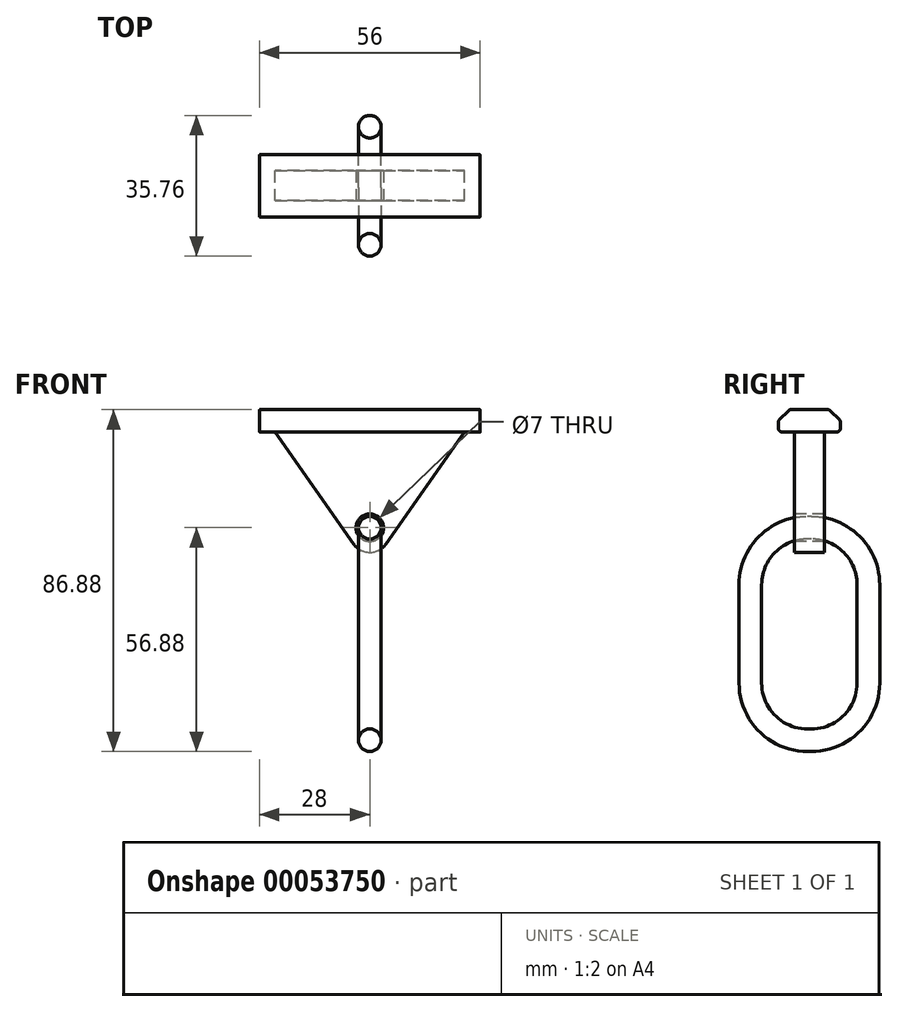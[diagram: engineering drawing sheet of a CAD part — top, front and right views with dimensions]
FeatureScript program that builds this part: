
annotation { "Feature Type Name" : "Feature", "Feature Type Description" : "" }
export const myFeature = defineFeature(function(context is Context, id is Id, definition is map)
    precondition{}
    {
        {
            var Q0;
            Q0=qCreatedBy(makeId("Right.planeOp"),FACE);
            var sketch = newSketch(context, id + "F0", { "sketchPlane" : qUnion([Q0])});
            skLineSegment(sketch, "E0", {"start": v(-5.05, 0) * mm, "end": v(5.05, 0) * mm});
            skLineSegment(sketch, "E1", {"start": v(-7.9, -5.7) * mm, "end": v(7.9, -5.7) * mm});
            skLineSegment(sketch, "E2", {"start": v(0, 0) * mm, "end": v(0, -5.7) * mm});
            skLineSegment(sketch, "E3", {"start": v(-7.9, -5.7) * mm, "end": v(-7.9, -2.85) * mm});
            skLineSegment(sketch, "E4", {"start": v(7.9, -5.7) * mm, "end": v(7.9, -2.85) * mm});
            skLineSegment(sketch, "E5", {"start": v(7.9, -2.85) * mm, "end": v(5.05, 0) * mm});
            skLineSegment(sketch, "E6", {"start": v(-7.9, -2.85) * mm, "end": v(-5.05, 0) * mm});
            skSolve(sketch);
        }
        {
            var Q0;
            Q0 = qSketchRegion(id + "F0", true);
            extrude(context, id + "F1", {"entities" : qUnion([Q0]), "endBound" : BoundingType.SYMMETRIC, "depth" : 56 * mm});
        }
        {
            var Q0;
            Q0=makeQuery(id+"F1.opExtrude","SWEPT_EDGE",EDGE,{"disambiguationData":[OSD([sQuery(id+"F0.wireOp",EDGE,"E0"),sQuery(id+"F0.wireOp",EDGE,"E6")])]});
            var Q1;
            Q1=makeQuery(id+"F1.opExtrude","SWEPT_EDGE",EDGE,{"disambiguationData":[OSD([sQuery(id+"F0.wireOp",EDGE,"E3"),sQuery(id+"F0.wireOp",EDGE,"E6")])]});
            var Q2;
            Q2=makeQuery(id+"F1.opExtrude","SWEPT_EDGE",EDGE,{"disambiguationData":[OSD([sQuery(id+"F0.wireOp",EDGE,"E1"),sQuery(id+"F0.wireOp",EDGE,"E3")])]});
            var Q3;
            Q3=makeQuery(id+"F1.opExtrude","SWEPT_EDGE",EDGE,{"disambiguationData":[OSD([sQuery(id+"F0.wireOp",EDGE,"E0"),sQuery(id+"F0.wireOp",EDGE,"E5")])]});
            var Q4;
            Q4=makeQuery(id+"F1.opExtrude","SWEPT_EDGE",EDGE,{"disambiguationData":[OSD([sQuery(id+"F0.wireOp",EDGE,"E4"),sQuery(id+"F0.wireOp",EDGE,"E5")])]});
            var Q5;
            Q5=makeQuery(id+"F1.opExtrude","SWEPT_EDGE",EDGE,{"disambiguationData":[OSD([sQuery(id+"F0.wireOp",EDGE,"E1"),sQuery(id+"F0.wireOp",EDGE,"E4")])]});
            fillet(context, id + "F2", {"entities" : qUnion([Q0, Q1, Q2, Q3, Q4, Q5]), "radius" : 1 * mm, "tangentPropagation" : true, "allowEdgeOverflow" : false});
        }
        {
            var Q0;
            Q0=qCreatedBy(makeId("Front.planeOp"),FACE);
            var sketch = newSketch(context, id + "F3", { "sketchPlane" : qUnion([Q0])});
            skLineSegment(sketch, "E7", {"start": v(-24.02, -5.7) * mm, "end": v(24.02, -5.7) * mm});
            skLineSegment(sketch, "E8", {"start": v(24.02, -5.7) * mm, "end": v(0, -40) * mm});
            skLineSegment(sketch, "E9", {"start": v(0, -40) * mm, "end": v(-24.02, -5.7) * mm});
            skSolve(sketch);
        }
        {
            var Q0;
            Q0 = qSketchRegion(id + "F3", true);
            extrude(context, id + "F4", {"entities" : qUnion([Q0]), "operationType" : NewBodyOperationType.ADD, "endBound" : BoundingType.SYMMETRIC, "depth" : 7.6 * mm});
        }
        {
            var Q0;
            Q0=makeQuery(id+"F4.opExtrude","SWEPT_EDGE",EDGE,{"disambiguationData":[OSD([sQuery(id+"F3.wireOp",EDGE,"E8"),sQuery(id+"F3.wireOp",EDGE,"E9")])]});
            fillet(context, id + "F5", {"entities" : qUnion([Q0]), "radius" : 5 * mm, "tangentPropagation" : true, "allowEdgeOverflow" : false});
        }
        {
            var Q0;
            Q0=qCreatedBy(makeId("Front.planeOp"),FACE);
            var sketch = newSketch(context, id + "F6", { "sketchPlane" : qUnion([Q0])});
            skCircle(sketch, "E10", {"center": v(0, -30) * mm, "radius": 3.5 * mm});
            skSolve(sketch);
        }
        {
            var Q0;
            Q0 = qSketchRegion(id + "F6", true);
            extrude(context, id + "F7", {"entities" : qUnion([Q0]), "operationType" : NewBodyOperationType.REMOVE, "endBound" : BoundingType.SYMMETRIC, "oppositeDirection" : true, "depth" : 25 * mm});
        }
        {
            var Q0;
            Q0=qCreatedBy(makeId("Right.planeOp"),FACE);
            var sketch = newSketch(context, id + "F8", { "sketchPlane" : qUnion([Q0])});
            skLineSegment(sketch, "E11.bottom", {"start": v(-0.5, -30) * mm, "end": v(0.5, -30) * mm});
            skLineSegment(sketch, "E11.top", {"start": v(-0.5, -84) * mm, "end": v(0.5, -84) * mm});
            skLineSegment(sketch, "E11.left", {"start": v(-15, -44.5) * mm, "end": v(-15, -69.5) * mm});
            skLineSegment(sketch, "E11.right", {"start": v(15, -44.5) * mm, "end": v(15, -69.5) * mm});
            skPoint(sketch, "E12.visualSharp", {"position": v(-15, -30) * mm});
            skArc(sketch, "E12.filletArc", {"start": v(-0.5, -30) * mm, "mid": v(-10.75, -34.25) * mm, "end": v(-15, -44.5) * mm});
            skPoint(sketch, "E13.visualSharp", {"position": v(15, -30) * mm});
            skArc(sketch, "E13.filletArc", {"start": v(15, -44.5) * mm, "mid": v(10.75, -34.25) * mm, "end": v(0.5, -30) * mm});
            skPoint(sketch, "E14.visualSharp", {"position": v(-15, -84) * mm});
            skArc(sketch, "E14.filletArc", {"start": v(-15, -69.5) * mm, "mid": v(-10.75, -79.75) * mm, "end": v(-0.5, -84) * mm});
            skPoint(sketch, "E15.visualSharp", {"position": v(15, -84) * mm});
            skArc(sketch, "E15.filletArc", {"start": v(0.5, -84) * mm, "mid": v(10.75, -79.75) * mm, "end": v(15, -69.5) * mm});
            skSolve(sketch);
        }
        {
            var Q0;
            Q0=qCreatedBy(makeId("Front.planeOp"),FACE);
            var sketch = newSketch(context, id + "F9", { "sketchPlane" : qUnion([Q0])});
            skCircle(sketch, "E16", {"center": v(0, -30) * mm, "radius": 2.88 * mm});
            skSolve(sketch);
        }
        {
            var Q0;
            Q0 = qSketchRegion(id + "F9", true);
            var Q1;
            Q1 = qConstructionFilter(qBodyType(qCreatedBy(id + "F8" ,EDGE), BodyType.WIRE), ConstructionObject.NO);
            sweep(context, id + "F10", {"operationType" : NewBodyOperationType.ADD, "profiles" : qUnion([Q0]), "path" : qUnion([Q1])});
        }
    });
